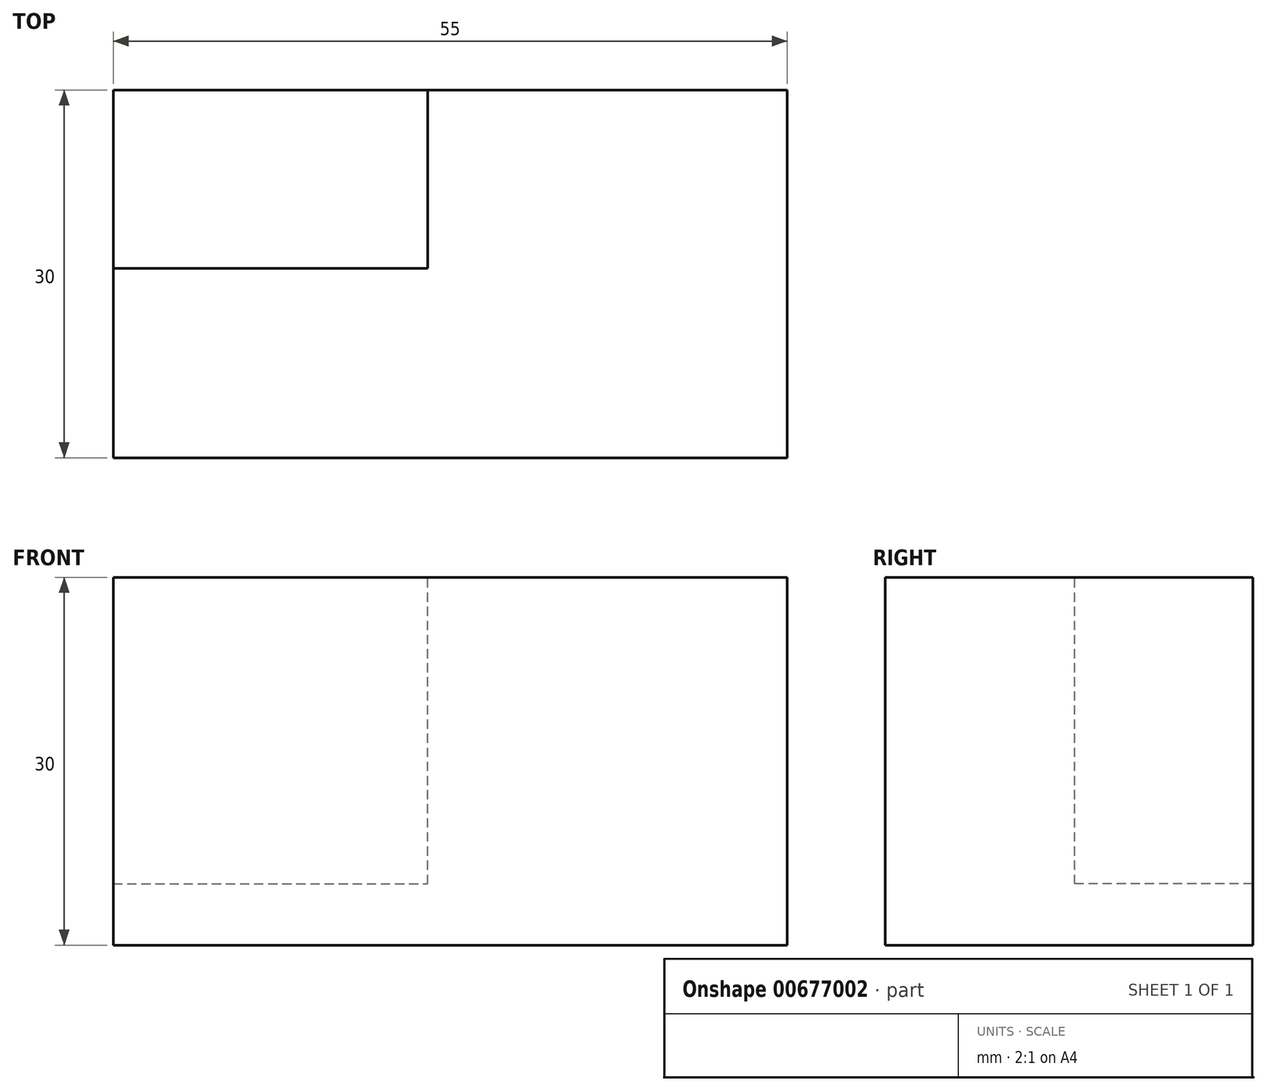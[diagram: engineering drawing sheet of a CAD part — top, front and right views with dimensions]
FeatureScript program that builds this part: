
annotation { "Feature Type Name" : "Feature", "Feature Type Description" : "" }
export const myFeature = defineFeature(function(context is Context, id is Id, definition is map)
    precondition{}
    {
        {
            var Q0;
            Q0=qCreatedBy(makeId("Top.planeOp"),FACE);
            var sketch = newSketch(context, id + "F0", { "sketchPlane" : qUnion([Q0])});
            skLineSegment(sketch, "E0.bottom", {"start": v(-25.68, 14.54) * mm, "end": v(29.32, 14.54) * mm});
            skLineSegment(sketch, "E0.top", {"start": v(-25.68, -15.46) * mm, "end": v(29.32, -15.46) * mm});
            skLineSegment(sketch, "E0.left", {"start": v(-25.68, 14.54) * mm, "end": v(-25.68, -15.46) * mm});
            skLineSegment(sketch, "E0.right", {"start": v(29.32, 14.54) * mm, "end": v(29.32, -15.46) * mm});
            skSolve(sketch);
        }
        {
            var Q0;
            Q0=makeQuery(id+"F0.imprint","IMPRINT",FACE,{"disambiguationData":[TD([[makeQuery(id+"F0.imprint","IMPRINT",EDGE,{"derivedFrom":sQuery(id+"F0.wireOp",EDGE,"E0.bottom")}),-1.0]])]});
            extrude(context, id + "F1", {"entities" : qUnion([Q0]), "depth" : 30 * mm, "offsetDistance" : 25 * mm});
        }
        {
            var Q0;
            Q0=makeQuery(id+"F1.opExtrude","CAP_FACE",FACE,{"disambiguationData":[OSD([sQuery(id+"F0.wireOp",EDGE,"E0.bottom"),sQuery(id+"F0.wireOp",EDGE,"E0.top"),sQuery(id+"F0.wireOp",EDGE,"E0.left"),sQuery(id+"F0.wireOp",EDGE,"E0.right")])],"isStart":false});
            var sketch = newSketch(context, id + "F2", { "sketchPlane" : qUnion([Q0])});
            skLineSegment(sketch, "E1", {"start": v(-25.68, 0) * mm, "end": v(0, 0) * mm});
            skPoint(sketch, "E1.startSnap0", {"position": v(-25.68, -0.46) * mm});
            skLineSegment(sketch, "E2", {"start": v(0, 0) * mm, "end": v(0, 14.54) * mm});
            skSolve(sketch);
        }
        {
            var Q0;
            {var subQ0=sQuery(id+"F2.wireOp",EDGE,"E1");Q0=makeQuery(id+"F2.imprint","IMPRINT",FACE,{"disambiguationData":[TD([[makeQuery(id+"F2.imprint","IMPRINT",EDGE,{"derivedFrom":subQ0}),1.0]])]});}
            extrude(context, id + "F3", {"entities" : qUnion([Q0]), "operationType" : NewBodyOperationType.REMOVE, "oppositeDirection" : true, "depth" : 25 * mm, "offsetDistance" : 25 * mm});
        }
    });
